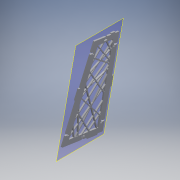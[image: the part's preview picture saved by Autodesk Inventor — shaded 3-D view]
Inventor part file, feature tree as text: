
AUTODESK INVENTOR PART (.ipt)
format: ipt  version: 2019 (Build 230136000, 136)  size: 1,385,472 bytes
history: native  units: in
note: dims shown in document units (in); Inventor stores cm internally (conversion verified against a paired STEP export)
features: reference x12, fillet x11, other x11, extrude x10, sketch x5, plane x1
ambient origin geometry x8: Origin, YZ Plane, XZ Plane, XY Plane, X Axis, Y Axis, Z Axis, Center Point
bodies: Solid1 (feature_tree)
feature tree (50):
  plane  "Work Plane1"
  extrude  "SidePanel"  Depth=0.0394in
  fillet  "CornerFillet"  Radius=0.475in
  extrude  "ScrewSlots"  Depth=0.475in
  fillet  "SlotFillets"  Radius=0.1495in
  extrude  "TopTab"  Depth=0.1495in
  fillet  "TopTabFillet"  Radius=0.475in
  extrude  "BottomTab"  Depth=0.3265in
  fillet  "BottomTabFillet"  Radius=0.1234in
  extrude  "BackTab"  Depth=0.1234in
  fillet  "BackTabFillet"  Radius=0.3265in
  extrude  "FrontTab"  Depth=0.1234in
  fillet  "FrontTabFillet"  Radius=0.3265in
  extrude  "InsideGap"  Depth=0.1234in
  fillet  "InsideGapFillet"  Radius=0.475in
  extrude  "Hash1"  Depth=0.1495in
  extrude  "Hash2"  Depth=0.3265in
  fillet  "GridFillets1"  Radius=0.1234in
  fillet  "GridFillets2"  Radius=0.1495in
  fillet  "GridFillets3"  Radius=0.475in
  extrude  "SmallHoleFill"  Depth=0.3265in
  fillet  "GridFillet4"  Radius=0.1234in
  sketch  "Sketch1"  dims[d0=0.125in d1=0.0in d2=0.0394in d7=0.475in]
  other  "ScrewSketch"
  reference  "Reference1"
  reference  "Reference2"
  reference  "Reference3"
  reference  "Reference4"
  other  "TopTabSketch"
  other  "BottomTabSketch"
  other  "BackTabSketch"
  other  "FrontTabSketch"
  sketch  "Sketch7"  dims[d8=0.1495in d10=0.475in d11=0.1495in]
  reference  "Reference30"
  reference  "Reference31"
  reference  "Reference32"
  reference  "Reference33"
  reference  "Reference34"
  reference  "Reference35"
  reference  "Reference36"
  reference  "Reference37"
  sketch  "Sketch8"  dims[d14=0.475in d17=0.1495in d18=0.475in]
  sketch  "Sketch9"  dims[d20=0.1495in d21=0.3265in d22=0.1234in]
  sketch  "Sketch10"  dims[d23=0.3265in d24=0.1234in d25=0.3265in d26=0.1234in d27=0.3265in d28=0.1234in d29=0.475in d30=0.1495in d31=0.3265in d32=0.1234in d33=0.1495in d34=0.475in d35=0.3265in d36=0.1234in d37=1.0in d38=0.0in d39=0.0197in d40=1.0in d41=1.0in d42=1.0in d43=1.0in d44=1.0in d47=0.125in d48=0.0in d49=0.0197in d50=1.0in d53=0.125in d54=0.0in d55=0.0197in d56=1.0in d58=0.125in d59=0.0in d60=0.0197in d61=0.375in d63=0.125in d64=0.0in d65=0.0197in d66=0.5in d67=0.5in d68=0.5in d69=0.5in d70=0.5in d71=0.5in d72=0.5in d73=0.5in d74=0.125in d75=0.0in d76=0.0197in d77=60.0deg d78=0.939in d79=1.515in d80=0.4358in d81=2.139in d82=0.5045in d83=0.215in d84=1.0133in d85=1.546in d86=1.0545in d87=3.453in d88=1.0133in d89=0.8452in d90=3.873in d91=4.753in d92=1.0376in d93=5.4in d94=0.9139in d95=6.236in d96=1.0857in d97=0.08in d98=0.08in d99=0.08in d100=0.08in d101=0.08in d102=0.08in d103=0.08in d104=0.08in d106=0.08in d107=0.08in d108=0.125in d109=0.0in d110=1.267in d111=0.1594in d112=2.361in d113=0.2789in d114=2.858in d115=0.1251in d116=3.453in d117=0.3357in d118=4.637in d119=0.2125in d120=5.689in d121=0.2915in d122=6.786in d123=0.4154in d124=7.845in d125=45.0deg d126=0.514in d127=0.8658in d128=0.08in d129=0.08in d131=0.08in d132=0.08in d133=0.08in d134=0.08in d135=0.08in d136=0.08in d137=0.08in d138=0.125in d139=0.0in d140=0.0197in d141=0.0197in d142=0.0197in d143=0.125in d144=0.0in d145=0.0197in]
  parser-record x1  (decoder bookkeeping rows leaked as tree rows — omitted from the tree; the rows remain in map.json)
  other  "ArcadeController.iam"
  other  "TopPanel:1"
  other  "BottomPanel:1"
  other  "Panel_back:1"
  other  "Panel_front:1"
note: 1 file-system path scrubbed to <path> (originals preserved in map.json)
